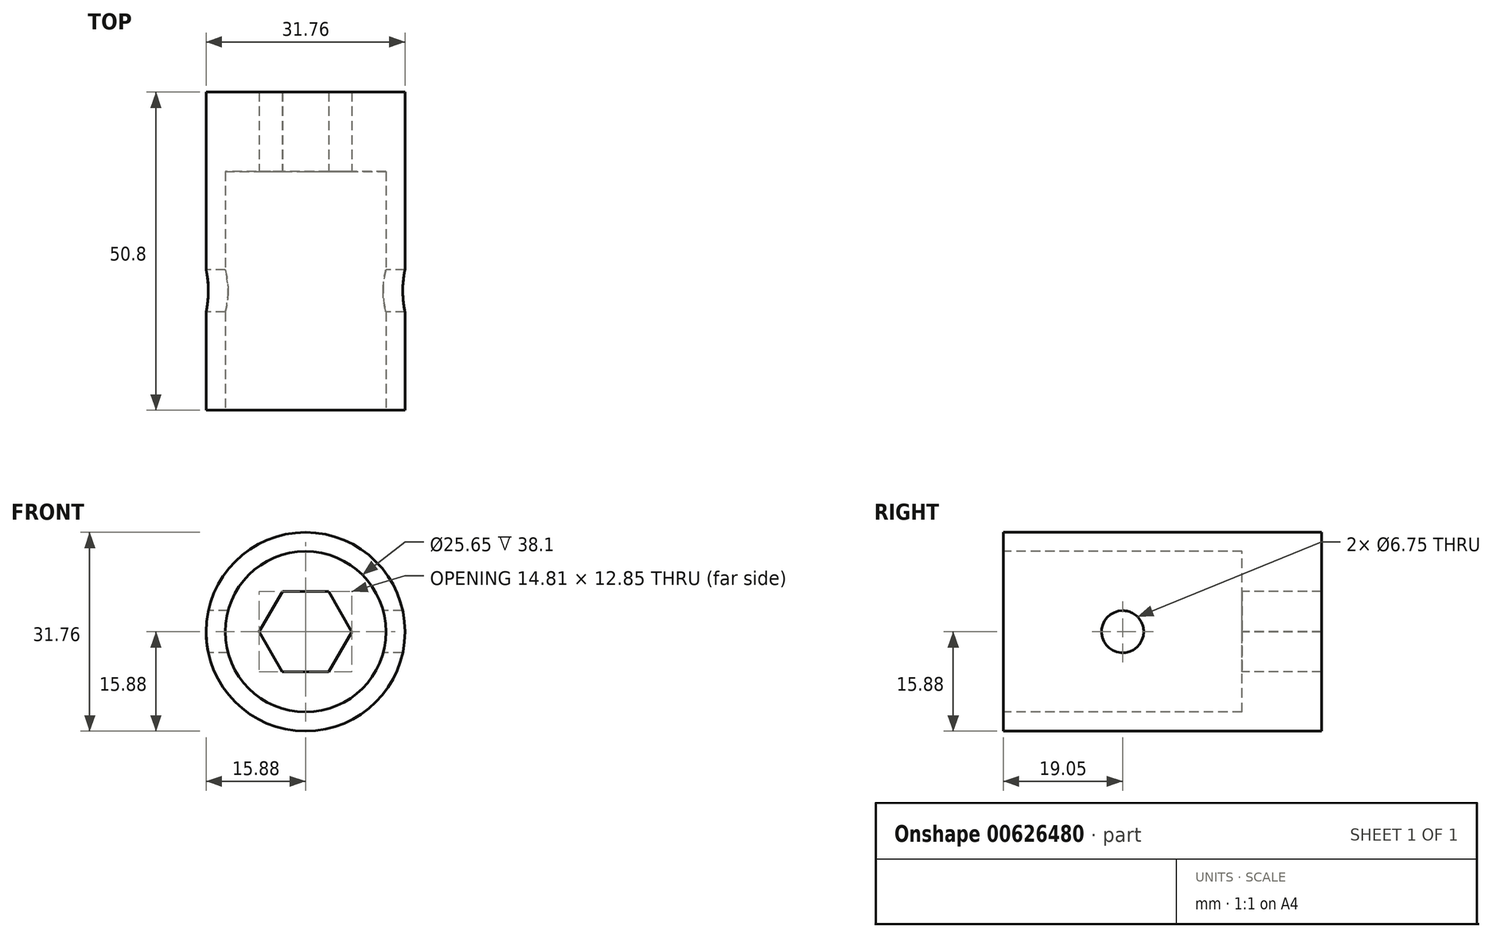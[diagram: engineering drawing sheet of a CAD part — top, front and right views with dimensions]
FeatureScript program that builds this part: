
annotation { "Feature Type Name" : "Feature", "Feature Type Description" : "" }
export const myFeature = defineFeature(function(context is Context, id is Id, definition is map)
    precondition{}
    {
        {
            var Q0;
            Q0=qCreatedBy(makeId("Front.planeOp"),FACE);
            var sketch = newSketch(context, id + "F0", { "sketchPlane" : qUnion([Q0])});
            skCircle(sketch, "E0", {"center": v(0, 0) * mm, "radius": 15.88 * mm});
            skSolve(sketch);
        }
        {
            var Q0;
            Q0=makeQuery(id+"F0.imprint","IMPRINT",FACE,{"disambiguationData":[TD([[makeQuery(id+"F0.imprint","IMPRINT",EDGE,{"derivedFrom":sQuery(id+"F0.wireOp",EDGE,"E0")}),1.0]])]});
            extrude(context, id + "F1", {"entities" : qUnion([Q0]), "depth" : 50.8 * mm, "offsetDistance" : 25.4 * mm});
        }
        {
            var Q0;
            Q0=makeQuery(id+"F1.opExtrude","CAP_FACE",FACE,{"disambiguationData":[OSD([sQuery(id+"F0.wireOp",EDGE,"E0")])],"isStart":false});
            var sketch = newSketch(context, id + "F2", { "sketchPlane" : qUnion([Q0])});
            skCircle(sketch, "E1", {"center": v(0, 0) * mm, "radius": 12.83 * mm});
            skSolve(sketch);
        }
        {
            var Q0;
            Q0=makeQuery(id+"F2.imprint","IMPRINT",FACE,{"disambiguationData":[TD([[makeQuery(id+"F2.imprint","IMPRINT",EDGE,{"derivedFrom":sQuery(id+"F2.wireOp",EDGE,"E1")}),1.0]])]});
            extrude(context, id + "F3", {"entities" : qUnion([Q0]), "operationType" : NewBodyOperationType.REMOVE, "oppositeDirection" : true, "depth" : 38.1 * mm, "offsetDistance" : 25.4 * mm});
        }
        {
            var Q0;
            Q0=makeQuery(id+"F3.boolean.opBoolean","COPY",FACE,{"derivedFrom":makeQuery(id+"F3.opExtrude","CAP_FACE",FACE,{"disambiguationData":[OSD([sQuery(id+"F2.wireOp",EDGE,"E1")])],"isStart":false})});
            var sketch = newSketch(context, id + "F4", { "sketchPlane" : qUnion([Q0])});
            skCircle(sketch, "E2.cCircle", {"center": v(0, 0) * mm, "radius": 6.41 * mm, "construction": true});
            skLineSegment(sketch, "E2.0", {"start": v(3.72, 6.4) * mm, "end": v(7.4, -0.02) * mm});
            skLineSegment(sketch, "E2.1", {"start": v(7.4, -0.02) * mm, "end": v(3.68, -6.42) * mm});
            skLineSegment(sketch, "E2.2", {"start": v(3.68, -6.42) * mm, "end": v(-3.72, -6.4) * mm});
            skLineSegment(sketch, "E2.3", {"start": v(-3.72, -6.4) * mm, "end": v(-7.4, 0.02) * mm});
            skLineSegment(sketch, "E2.4", {"start": v(-7.4, 0.02) * mm, "end": v(-3.68, 6.42) * mm});
            skLineSegment(sketch, "E2.5", {"start": v(-3.68, 6.42) * mm, "end": v(3.72, 6.4) * mm});
            skPoint(sketch, "E2.0.midPoint", {"position": v(5.56, 3.19) * mm});
            skSolve(sketch);
        }
        {
            var Q0;
            Q0=makeQuery(id+"F4.imprint","IMPRINT",FACE,{"disambiguationData":[TD([[makeQuery(id+"F4.imprint","IMPRINT",EDGE,{"derivedFrom":sQuery(id+"F4.wireOp",EDGE,"E2.0")}),-1.0]])]});
            extrude(context, id + "F5", {"entities" : qUnion([Q0]), "operationType" : NewBodyOperationType.REMOVE, "oppositeDirection" : true, "depth" : 12.7 * mm, "offsetDistance" : 25.4 * mm});
        }
        {
            var Q0;
            Q0=qCreatedBy(makeId("Right.planeOp"),FACE);
            var sketch = newSketch(context, id + "F6", { "sketchPlane" : qUnion([Q0])});
            skCircle(sketch, "E3", {"center": v(-31.75, 0) * mm, "radius": 3.37 * mm});
            skSolve(sketch);
        }
        {
            var Q0;
            Q0=qSketchRegion(id+"F6",true);
            extrude(context, id + "F7", {"entities" : qUnion([Q0]), "operationType" : NewBodyOperationType.REMOVE, "endBound" : BoundingType.SYMMETRIC, "depth" : 31.75 * mm, "offsetDistance" : 25.4 * mm});
        }
    });
